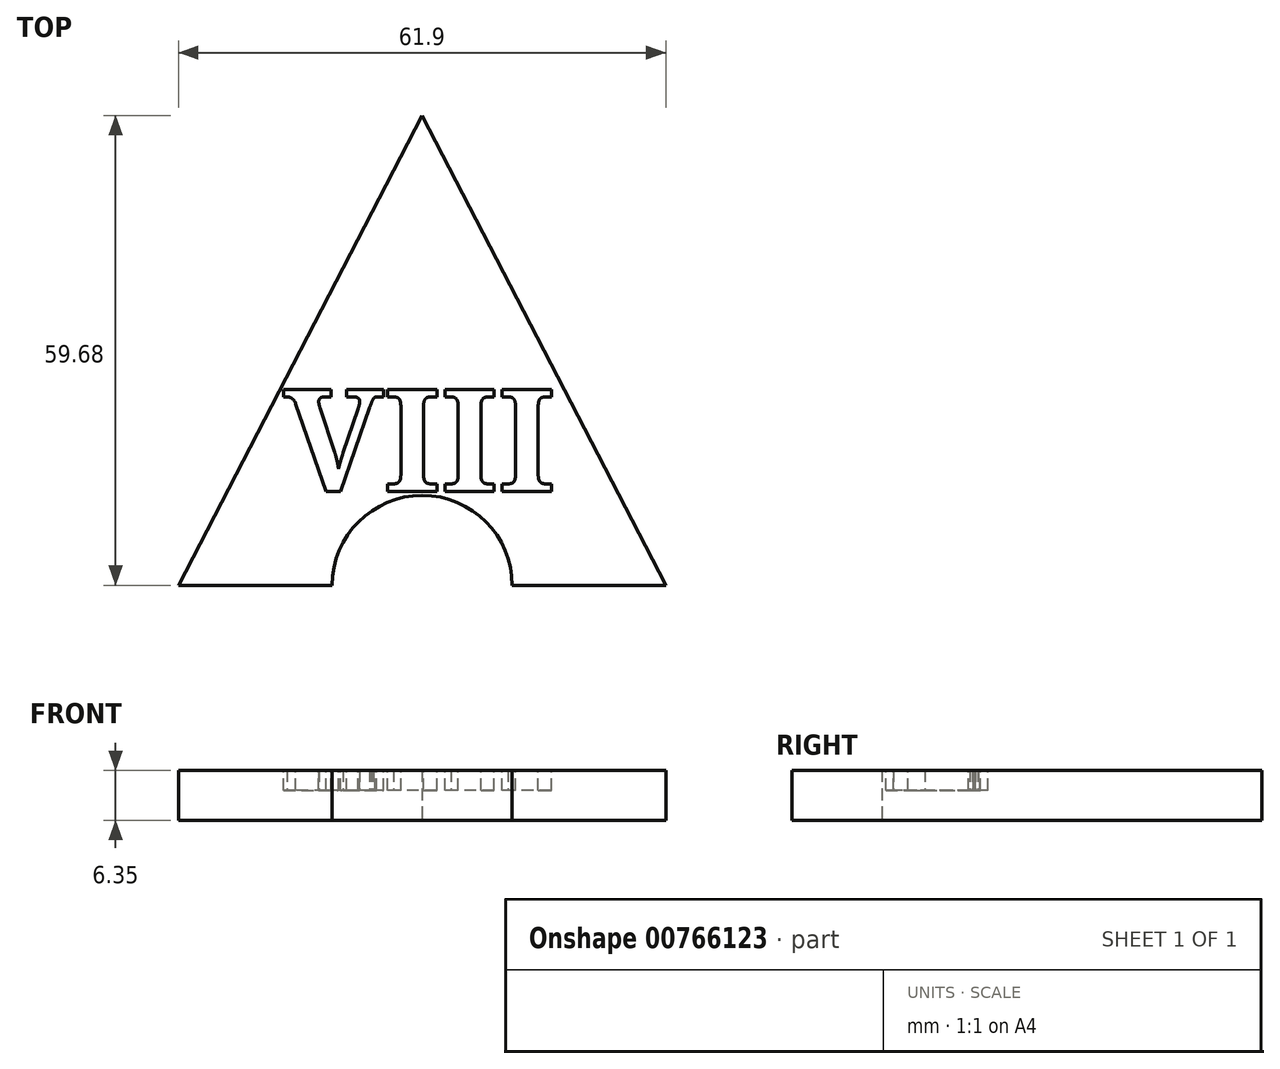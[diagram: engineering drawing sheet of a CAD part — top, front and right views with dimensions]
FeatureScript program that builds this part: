
annotation { "Feature Type Name" : "Feature", "Feature Type Description" : "" }
export const myFeature = defineFeature(function(context is Context, id is Id, definition is map)
    precondition{}
    {
        {
            var Q0;
            Q0=qCreatedBy(makeId("Top.planeOp"),FACE);
            var sketch = newSketch(context, id + "F0", { "sketchPlane" : qUnion([Q0])});
            skCircle(sketch, "E0.cCircle", {"center": v(0, 0) * mm, "radius": 12.73 * mm, "construction": true});
            skLineSegment(sketch, "E0.0", {"start": v(30.95, -12.73) * mm, "end": v(-30.95, -12.73) * mm});
            skLineSegment(sketch, "E0.1", {"start": v(-30.95, -12.73) * mm, "end": v(0, 46.95) * mm});
            skLineSegment(sketch, "E0.2", {"start": v(0, 46.95) * mm, "end": v(30.95, -12.73) * mm});
            skPoint(sketch, "E0.0.midPoint", {"position": v(0, -12.73) * mm});
            skSolve(sketch);
        }
        {
            var Q0;
            Q0=makeQuery(id+"F0.imprint","IMPRINT",FACE,{"disambiguationData":[TD([[makeQuery(id+"F0.imprint","IMPRINT",EDGE,{"derivedFrom":sQuery(id+"F0.wireOp",EDGE,"E0.0")}),-1.0]])]});
            extrude(context, id + "F1", {"entities" : qUnion([Q0]), "depth" : 6.35 * mm, "offsetDistance" : 25.4 * mm});
        }
        {
            var Q0;
            Q0=sQuery(id+"F0.wireOp",VERTEX,"E0.0.midPoint");
            var Q1;
            Q1=makeQuery(id+"F1.opExtrude","SWEPT_BODY",BODY,{"disambiguationData":[OSD([sQuery(id+"F0.wireOp",EDGE,"E0.0"),sQuery(id+"F0.wireOp",EDGE,"E0.1"),sQuery(id+"F0.wireOp",EDGE,"E0.2")])]});
            hole(context, id + "F2", {"style" : HoleStyle.SIMPLE, "endStyle" : HoleEndStyle.THROUGH, "oppositeDirection" : true, "holeDiameter" : 22.86 * mm, "majorDiameter" : 6.35 * mm, "isTappedThrough" : true, "tappedDepth" : 12.7 * mm, "tapClearance" : 3, "locations" : qUnion([Q0]), "scope" : qUnion([Q1])});
        }
        {
            var Q0;
            Q0=makeQuery(id+"F1.opExtrude","CAP_FACE",FACE,{"disambiguationData":[OSD([sQuery(id+"F0.wireOp",EDGE,"E0.0"),sQuery(id+"F0.wireOp",EDGE,"E0.1"),sQuery(id+"F0.wireOp",EDGE,"E0.2")])],"isStart":false});
            var sketch = newSketch(context, id + "F3", { "sketchPlane" : qUnion([Q0])});
            skText(sketch, "E1", { "text": "VIII", "fontName": "NotoSerif-Bold.ttf"});
            const initialGuessF3  = {"E1": [-0.0176, -0.0008, 1, 0, 0.01308]};
            skSetInitialGuess(sketch, initialGuessF3);
            skSolve(sketch);
        }
        {
            var Q0;
            Q0 = qSketchRegion(id + "F3", true);
            extrude(context, id + "F4", {"entities" : qUnion([Q0]), "operationType" : NewBodyOperationType.REMOVE, "oppositeDirection" : true, "depth" : 2.54 * mm, "offsetDistance" : 25.4 * mm});
        }
    });
